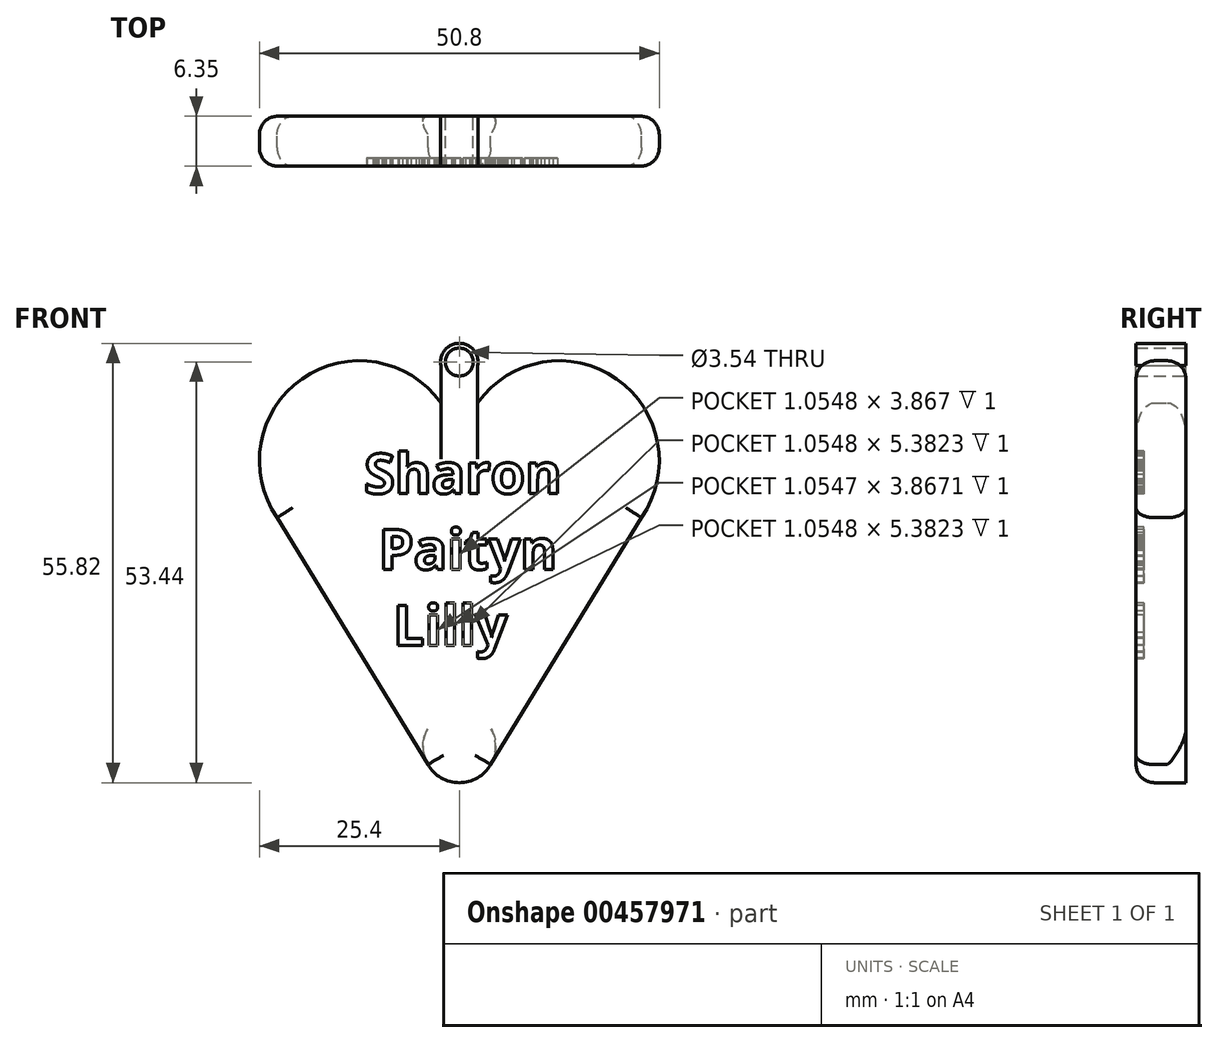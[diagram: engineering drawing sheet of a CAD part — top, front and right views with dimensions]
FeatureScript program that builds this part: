
annotation { "Feature Type Name" : "Feature", "Feature Type Description" : "" }
export const myFeature = defineFeature(function(context is Context, id is Id, definition is map)
    precondition{}
    {
        {
            var Q0;
            Q0=qCreatedBy(makeId("Front.planeOp"),FACE);
            var sketch = newSketch(context, id + "F0", { "sketchPlane" : qUnion([Q0])});
            skCircle(sketch, "E0", {"center": v(-12.7, -40.15) * mm, "radius": 12.7 * mm});
            skCircle(sketch, "E1", {"center": v(12.7, -40.15) * mm, "radius": 12.7 * mm});
            skCircle(sketch, "E2", {"center": v(0, -76.44) * mm, "radius": 4.6 * mm});
            skCircle(sketch, "E3", {"center": v(0, -27.61) * mm, "radius": 2.38 * mm});
            skLineSegment(sketch, "E4", {"start": v(-2.34, -28.04) * mm, "end": v(-2.34, -32.8) * mm});
            skLineSegment(sketch, "E5", {"start": v(-2.34, -32.8) * mm, "end": v(2.34, -32.8) * mm});
            skLineSegment(sketch, "E6", {"start": v(2.34, -32.8) * mm, "end": v(2.34, -28.04) * mm});
            skLineSegment(sketch, "E7", {"start": v(23.9, -46.13) * mm, "end": v(4, -78.74) * mm});
            skLineSegment(sketch, "E8", {"start": v(-23.9, -46.13) * mm, "end": v(-4, -78.74) * mm});
            skCircle(sketch, "E9", {"center": v(0, -27.61) * mm, "radius": 1.77 * mm});
            skSolve(sketch);
        }
        {
            var Q0;
            {var subQ0=sQuery(id+"F0.wireOp",EDGE,"c1dc9967-65be-475e-a1ab-9509db93362e");var subQ1=sQuery(id+"F0.wireOp",EDGE,"E0");var subQ2=makeQuery(id+"F0.imprint","INTERSECT",VERTEX,{"disambiguationData":[OD(0.0)],"derivedFrom":[subQ1,subQ0]});Q0=makeQuery(id+"F0.imprint","IMPRINT",FACE,{"disambiguationData":[TD([[makeQuery(id+"F0.imprint","IMPRINT",EDGE,{"disambiguationData":[TD([[subQ2,1.0]])],"derivedFrom":subQ1}),1.0]])]});}
            var Q1;
            {var subQ3=sQuery(id+"F0.wireOp",EDGE,"E1");var subQ5=sQuery(id+"F0.wireOp",EDGE,"E0");var subQ6=makeQuery(id+"F0.imprint","INTERSECT",VERTEX,{"derivedFrom":[subQ5,subQ3]});Q1=makeQuery(id+"F0.imprint","IMPRINT",FACE,{"disambiguationData":[TD([[makeQuery(id+"F0.imprint","IMPRINT",EDGE,{"disambiguationData":[TD([[subQ6,1.0]])],"derivedFrom":subQ5}),-1.0]])]});}
            var Q2;
            {var subQ0=sQuery(id+"F0.wireOp",EDGE,"E1");var subQ1=makeQuery(id+"F0.imprint","INTERSECT",VERTEX,{"derivedFrom":[sQuery(id+"F0.wireOp",EDGE,"E0"),subQ0]});Q2=makeQuery(id+"F0.imprint","IMPRINT",FACE,{"disambiguationData":[TD([[makeQuery(id+"F0.imprint","IMPRINT",EDGE,{"disambiguationData":[TD([[subQ1,-1.0]])],"derivedFrom":subQ0}),1.0]])]});}
            var Q3;
            {var subQ0=sQuery(id+"F0.wireOp",EDGE,"E2");var subQ1=makeQuery(id+"F0.imprint","INTERSECT",VERTEX,{"derivedFrom":[subQ0,sQuery(id+"F0.wireOp",EDGE,"22bdcb90-6837-4773-9a82-ad14b141443f")]});Q3=makeQuery(id+"F0.imprint","IMPRINT",FACE,{"disambiguationData":[TD([[makeQuery(id+"F0.imprint","IMPRINT",EDGE,{"disambiguationData":[TD([[subQ1,1.0]])],"derivedFrom":subQ0}),1.0]])]});}
            var Q4;
            {var subQ3=sQuery(id+"F0.wireOp",EDGE,"d9c96f0d-c952-4023-af67-c3b31cf93496");Q4=makeQuery(id+"F0.imprint","IMPRINT",FACE,{"disambiguationData":[TD([[makeQuery(id+"F0.imprint","IMPRINT",EDGE,{"derivedFrom":subQ3}),1.0]])]});}
            var Q5;
            {var subQ0=sQuery(id+"F0.wireOp",EDGE,"43af675b-4bb7-419d-b6aa-33dcd8a345be");Q5=makeQuery(id+"F0.imprint","IMPRINT",FACE,{"disambiguationData":[TD([[makeQuery(id+"F0.imprint","IMPRINT",EDGE,{"derivedFrom":subQ0}),1.0]])]});}
            extrude(context, id + "F1", {"entities" : qUnion([Q0, Q1, Q2, Q3, Q4, Q5]), "depth" : 1 / 203.2 * mm});
        }
        {
            var Q0;
            Q0 = qSketchRegion(id + "F0", true);
            var Q1;
            Q1=makeQuery(id+"F0.imprint","IMPRINT",FACE,{"disambiguationData":[TD([[makeQuery(id+"F0.imprint","IMPRINT",EDGE,{"derivedFrom":sQuery(id+"F0.wireOp",EDGE,"E3")}),-1.0]])]});
            extrude(context, id + "F2", {"entities" : qUnion([Q0, Q1]), "operationType" : NewBodyOperationType.ADD, "depth" : 6.35 * mm});
        }
        {
            var Q0;
            Q0=makeQuery(id+"F2.opExtrude","CAP_FACE",FACE,{"disambiguationData":[OSD([sQuery(id+"F0.wireOp",EDGE,"E0"),sQuery(id+"F0.wireOp",EDGE,"E1"),sQuery(id+"F0.wireOp",EDGE,"E2"),sQuery(id+"F0.wireOp",EDGE,"E4"),sQuery(id+"F0.wireOp",EDGE,"E6"),sQuery(id+"F0.wireOp",EDGE,"E3"),sQuery(id+"F0.wireOp",EDGE,"E7"),sQuery(id+"F0.wireOp",EDGE,"E8"),sQuery(id+"F0.wireOp",EDGE,"E9")])],"isStart":false});
            var sketch = newSketch(context, id + "F3", { "sketchPlane" : qUnion([Q0])});
            skText(sketch, "E10", { "text": "Sharon\n Paityn\n  Lilly", "fontName": "OpenSans-Bold.ttf"});
            const initialGuessF3  = {"E10": [-0.01208, -0.04432, 1, 0, 0.0051]};
            skSetInitialGuess(sketch, initialGuessF3);
            skSolve(sketch);
        }
        {
            var Q0;
            Q0 = qSketchRegion(id + "F3", true);
            extrude(context, id + "F4", {"entities" : qUnion([Q0]), "operationType" : NewBodyOperationType.REMOVE, "oppositeDirection" : true, "depth" : 1 * mm, "offsetDistance" : 25 * mm});
        }
        {
            var Q0;
            Q0=makeQuery(id+"F2.opExtrude","CAP_EDGE",EDGE,{"disambiguationData":[OSD([sQuery(id+"F0.wireOp",EDGE,"E0")])],"isStart":false});
            var Q1;
            Q1=makeQuery(id+"F2.opExtrude","CAP_EDGE",EDGE,{"disambiguationData":[OSD([sQuery(id+"F0.wireOp",EDGE,"E1")])],"isStart":false});
            var Q2;
            {var subQ0=sQuery(id+"F0.wireOp",EDGE,"E1");Q2=makeQuery(id+"F2.boolean.opBoolean","MERGE",EDGE,{"derivedFrom":[makeQuery(id+"F1.opExtrude","CAP_EDGE",EDGE,{"disambiguationData":[OSD([subQ0])],"isStart":true}),makeQuery(id+"F2.opExtrude","CAP_EDGE",EDGE,{"disambiguationData":[OSD([subQ0])],"isStart":true})]});}
            var Q3;
            Q3=makeQuery(id+"F2.opExtrude","CAP_EDGE",EDGE,{"disambiguationData":[OSD([sQuery(id+"F0.wireOp",EDGE,"E0")])],"isStart":true});
            var Q4;
            Q4=makeQuery(id+"F2.opExtrude","CAP_EDGE",EDGE,{"disambiguationData":[OSD([sQuery(id+"F0.wireOp",EDGE,"E2")])],"isStart":true});
            var Q5;
            Q5=makeQuery(id+"F2.opExtrude","CAP_EDGE",EDGE,{"disambiguationData":[OSD([sQuery(id+"F0.wireOp",EDGE,"E2")])],"isStart":false});
            fillet(context, id + "F5", {"entities" : qUnion([Q0, Q1, Q2, Q3, Q4, Q5]), "radius" : 2.34 * mm, "tangentPropagation" : true, "allowEdgeOverflow" : false});
        }
    });
